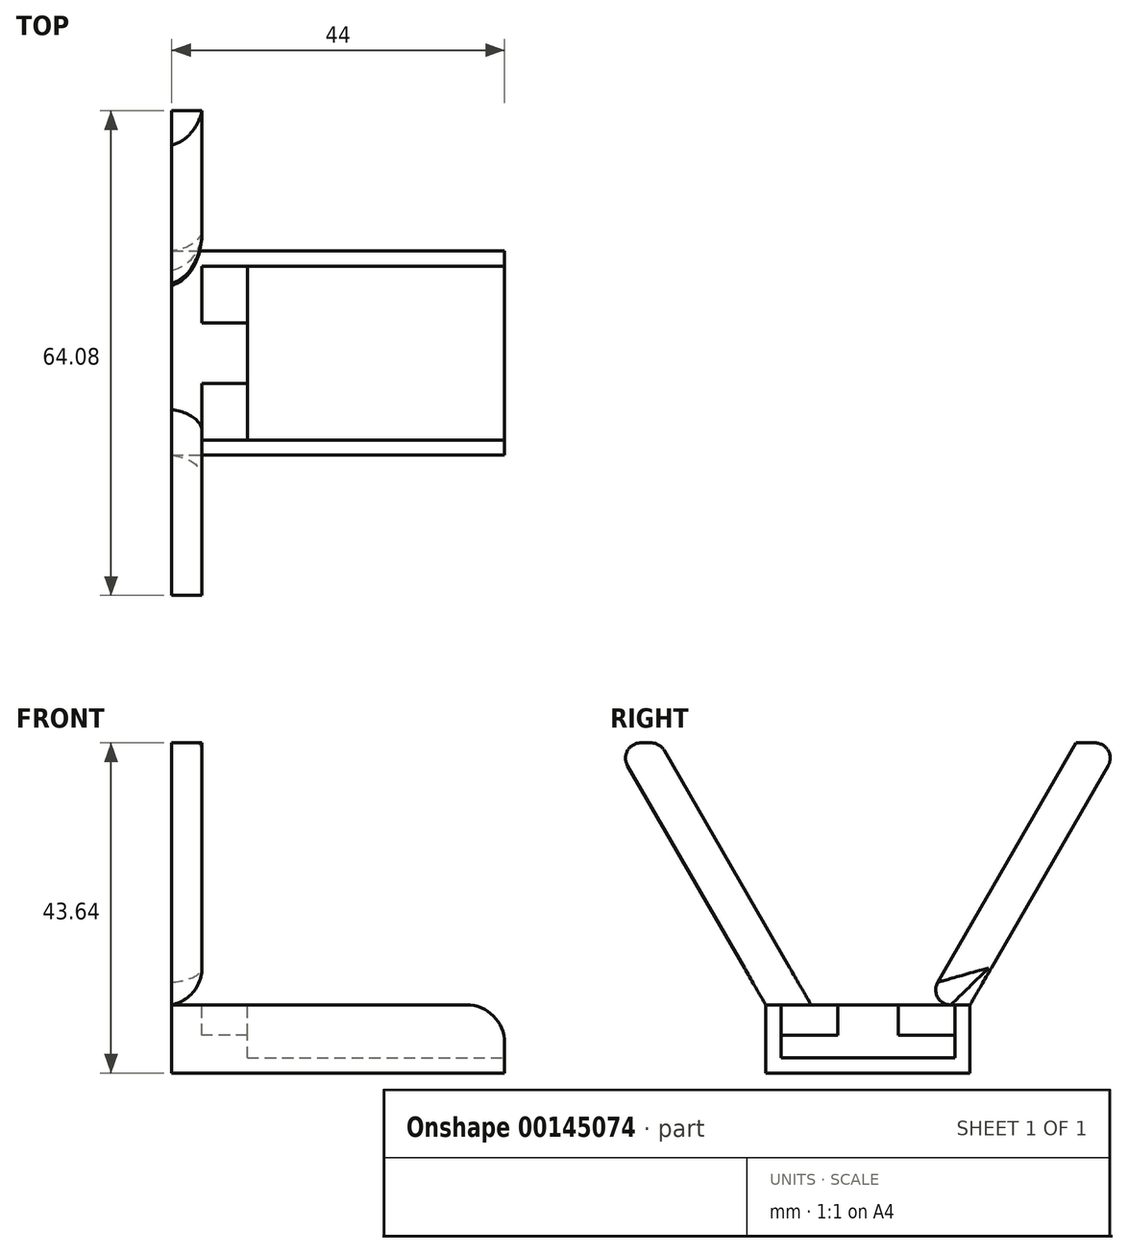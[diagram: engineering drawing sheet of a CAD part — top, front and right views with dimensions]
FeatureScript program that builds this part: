
annotation { "Feature Type Name" : "Feature", "Feature Type Description" : "" }
export const myFeature = defineFeature(function(context is Context, id is Id, definition is map)
    precondition{}
    {
        {
            var Q0;
            Q0=qCreatedBy(makeId("Top.planeOp"),FACE);
            var sketch = newSketch(context, id + "F0", { "sketchPlane" : qUnion([Q0])});
            skLineSegment(sketch, "E0.bottom", {"start": v(-23, 13.5) * mm, "end": v(21, 13.5) * mm});
            skLineSegment(sketch, "E0.top", {"start": v(-23, -13.5) * mm, "end": v(21, -13.5) * mm});
            skLineSegment(sketch, "E0.left", {"start": v(-23, 13.5) * mm, "end": v(-23, -13.5) * mm});
            skLineSegment(sketch, "E0.right", {"start": v(21, 13.5) * mm, "end": v(21, -13.5) * mm});
            skSolve(sketch);
        }
        {
            var Q0;
            Q0 = qSketchRegion(id + "F0", true);
            extrude(context, id + "F1", {"entities" : qUnion([Q0]), "oppositeDirection" : true, "depth" : 9 * mm});
        }
        {
            var Q0;
            Q0=qCreatedBy(makeId("Top.planeOp"),FACE);
            var sketch = newSketch(context, id + "F2", { "sketchPlane" : qUnion([Q0])});
            skLineSegment(sketch, "E1.bottom", {"start": v(-13, 11.5) * mm, "end": v(21, 11.5) * mm});
            skLineSegment(sketch, "E1.top", {"start": v(-13, -11.5) * mm, "end": v(21, -11.5) * mm});
            skLineSegment(sketch, "E1.left", {"start": v(-13, 11.5) * mm, "end": v(-13, -11.5) * mm});
            skLineSegment(sketch, "E1.right", {"start": v(21, 11.5) * mm, "end": v(21, -11.5) * mm});
            skSolve(sketch);
        }
        {
            var Q0;
            Q0 = qSketchRegion(id + "F2", true);
            extrude(context, id + "F3", {"entities" : qUnion([Q0]), "oppositeDirection" : true, "depth" : 7 * mm});
        }
        {
            var Q0;
            Q0=makeQuery(id+"F3.opExtrude","SWEPT_BODY",BODY,{"disambiguationData":[OSD([sQuery(id+"F2.wireOp",EDGE,"E1.bottom"),sQuery(id+"F2.wireOp",EDGE,"E1.top"),sQuery(id+"F2.wireOp",EDGE,"E1.left"),sQuery(id+"F2.wireOp",EDGE,"E1.right")])]});
            var Q1;
            Q1=makeQuery(id+"F1.opExtrude","SWEPT_BODY",BODY,{"disambiguationData":[OSD([sQuery(id+"F0.wireOp",EDGE,"E0.bottom"),sQuery(id+"F0.wireOp",EDGE,"E0.top"),sQuery(id+"F0.wireOp",EDGE,"E0.left"),sQuery(id+"F0.wireOp",EDGE,"E0.right")])]});
            booleanBodies(context, id + "F4", {"operationType" : BooleanOperationType.SUBTRACTION, "tools" : qUnion([Q0]), "targets" : qUnion([Q1])});
        }
        {
            var Q0;
            Q0=qCreatedBy(makeId("Top.planeOp"),FACE);
            var sketch = newSketch(context, id + "F5", { "sketchPlane" : qUnion([Q0])});
            skLineSegment(sketch, "E2.bottom", {"start": v(-13, 11.5) * mm, "end": v(-19, 11.5) * mm});
            skLineSegment(sketch, "E2.top", {"start": v(-13, 4) * mm, "end": v(-19, 4) * mm});
            skLineSegment(sketch, "E2.left", {"start": v(-13, 11.5) * mm, "end": v(-13, 4) * mm});
            skLineSegment(sketch, "E2.right", {"start": v(-19, 11.5) * mm, "end": v(-19, 4) * mm});
            skSolve(sketch);
        }
        {
            var Q0;
            Q0=qCreatedBy(makeId("Top.planeOp"),FACE);
            var sketch = newSketch(context, id + "F6", { "sketchPlane" : qUnion([Q0])});
            skLineSegment(sketch, "E3.bottom", {"start": v(-13, -4) * mm, "end": v(-19, -4) * mm});
            skLineSegment(sketch, "E3.top", {"start": v(-13, -11.5) * mm, "end": v(-19, -11.5) * mm});
            skLineSegment(sketch, "E3.left", {"start": v(-13, -4) * mm, "end": v(-13, -11.5) * mm});
            skLineSegment(sketch, "E3.right", {"start": v(-19, -4) * mm, "end": v(-19, -11.5) * mm});
            skSolve(sketch);
        }
        {
            var Q0;
            Q0 = qSketchRegion(id + "F6", true);
            var Q1;
            Q1 = qSketchRegion(id + "F5", true);
            extrude(context, id + "F7", {"entities" : qUnion([Q0, Q1]), "oppositeDirection" : true, "depth" : 4 * mm});
        }
        {
            var Q0;
            Q0=makeQuery(id+"F7.opExtrude","SWEPT_BODY",BODY,{"disambiguationData":[OSD([sQuery(id+"F5.wireOp",EDGE,"E2.bottom"),sQuery(id+"F5.wireOp",EDGE,"E2.top"),sQuery(id+"F5.wireOp",EDGE,"E2.left"),sQuery(id+"F5.wireOp",EDGE,"E2.right")])]});
            var Q1;
            Q1=makeQuery(id+"F7.opExtrude","SWEPT_BODY",BODY,{"disambiguationData":[OSD([sQuery(id+"F6.wireOp",EDGE,"E3.bottom"),sQuery(id+"F6.wireOp",EDGE,"E3.top"),sQuery(id+"F6.wireOp",EDGE,"E3.left"),sQuery(id+"F6.wireOp",EDGE,"E3.right")])]});
            var Q2;
            Q2=makeQuery(id+"F1.opExtrude","SWEPT_BODY",BODY,{"disambiguationData":[OSD([sQuery(id+"F0.wireOp",EDGE,"E0.bottom"),sQuery(id+"F0.wireOp",EDGE,"E0.top"),sQuery(id+"F0.wireOp",EDGE,"E0.left"),sQuery(id+"F0.wireOp",EDGE,"E0.right")])]});
            booleanBodies(context, id + "F8", {"operationType" : BooleanOperationType.SUBTRACTION, "tools" : qUnion([Q0, Q1]), "targets" : qUnion([Q2])});
        }
        {
            var Q0;
            Q0=makeQuery(id+"F1.opExtrude","SWEPT_FACE",FACE,{"disambiguationData":[OSD([sQuery(id+"F0.wireOp",EDGE,"E0.left")])]});
            var sketch = newSketch(context, id + "F9", { "sketchPlane" : qUnion([Q0])});
            skLineSegment(sketch, "E4", {"start": v(13.5, 0) * mm, "end": v(33.5, 34.64) * mm});
            skLineSegment(sketch, "E5", {"start": v(33.5, 34.64) * mm, "end": v(-33.5, 34.64) * mm});
            skLineSegment(sketch, "E6", {"start": v(-33.5, 34.64) * mm, "end": v(-13.5, 0) * mm});
            skLineSegment(sketch, "E7", {"start": v(-13.5, 0) * mm, "end": v(13.5, 0) * mm});
            skSolve(sketch);
        }
        {
            var Q0;
            Q0 = qSketchRegion(id + "F9", true);
            extrude(context, id + "F10", {"entities" : qUnion([Q0]), "oppositeDirection" : true, "depth" : 4 * mm});
        }
        {
            var Q0;
            Q0=makeQuery(id+"F9.imprint","IMPRINT",FACE,{"disambiguationData":[TD([[makeQuery(id+"F9.imprint","IMPRINT",EDGE,{"derivedFrom":sQuery(id+"F9.wireOp",EDGE,"E4")}),1.0]])]});
            var sketch = newSketch(context, id + "F11", { "sketchPlane" : qUnion([Q0])});
            skLineSegment(sketch, "E8", {"start": v(7.5, 0) * mm, "end": v(27.5, 34.64) * mm});
            skLineSegment(sketch, "E9", {"start": v(27.5, 34.64) * mm, "end": v(-27.5, 34.64) * mm});
            skLineSegment(sketch, "E10", {"start": v(-27.5, 34.64) * mm, "end": v(-7.5, 0) * mm});
            skLineSegment(sketch, "E11", {"start": v(-7.5, 0) * mm, "end": v(7.5, 0) * mm});
            skSolve(sketch);
        }
        {
            var Q0;
            Q0 = qSketchRegion(id + "F11", true);
            extrude(context, id + "F12", {"entities" : qUnion([Q0]), "oppositeDirection" : true, "depth" : 5 * mm});
        }
        {
            var Q0;
            Q0=makeQuery(id+"F12.opExtrude","SWEPT_BODY",BODY,{"disambiguationData":[OSD([sQuery(id+"F11.wireOp",EDGE,"E8"),sQuery(id+"F11.wireOp",EDGE,"E9"),sQuery(id+"F11.wireOp",EDGE,"E10"),sQuery(id+"F11.wireOp",EDGE,"E11")])]});
            var Q1;
            Q1=makeQuery(id+"F10.opExtrude","SWEPT_BODY",BODY,{"disambiguationData":[OSD([sQuery(id+"F9.wireOp",EDGE,"E4"),sQuery(id+"F9.wireOp",EDGE,"E5"),sQuery(id+"F9.wireOp",EDGE,"E6"),sQuery(id+"F9.wireOp",EDGE,"E7")])]});
            booleanBodies(context, id + "F13", {"operationType" : BooleanOperationType.SUBTRACTION, "tools" : qUnion([Q0]), "targets" : qUnion([Q1])});
        }
        {
            var Q0;
            Q0=makeQuery(id+"F10.opExtrude","SWEPT_EDGE",EDGE,{"disambiguationData":[OSD([sQuery(id+"F9.wireOp",EDGE,"E5"),sQuery(id+"F9.wireOp",EDGE,"E6")])]});
            var Q1;
            Q1=makeQuery(id+"F13.opBoolean","COPY",EDGE,{"derivedFrom":makeQuery(id+"F12.opExtrude","SWEPT_EDGE",EDGE,{"disambiguationData":[OSD([sQuery(id+"F9.wireOp",EDGE,"E5"),sQuery(id+"F11.wireOp",EDGE,"E9"),sQuery(id+"F11.wireOp",EDGE,"E10")])]})});
            var Q2;
            Q2=makeQuery(id+"F13.opBoolean","COPY",EDGE,{"derivedFrom":makeQuery(id+"F12.opExtrude","SWEPT_EDGE",EDGE,{"disambiguationData":[OSD([sQuery(id+"F9.wireOp",EDGE,"E5"),sQuery(id+"F11.wireOp",EDGE,"E8"),sQuery(id+"F11.wireOp",EDGE,"E9")])]})});
            var Q3;
            Q3=makeQuery(id+"F10.opExtrude","SWEPT_EDGE",EDGE,{"disambiguationData":[OSD([sQuery(id+"F9.wireOp",EDGE,"E4"),sQuery(id+"F9.wireOp",EDGE,"E5")])]});
            var Q4;
            Q4=makeQuery(id+"F13.opBoolean","COPY",EDGE,{"derivedFrom":makeQuery(id+"F12.opExtrude","SWEPT_EDGE",EDGE,{"disambiguationData":[OSD([sQuery(id+"F9.wireOp",EDGE,"E7"),sQuery(id+"F11.wireOp",EDGE,"E8"),sQuery(id+"F11.wireOp",EDGE,"E11")])]})});
            var Q5;
            Q5=makeQuery(id+"F13.opBoolean","COPY",EDGE,{"derivedFrom":makeQuery(id+"F12.opExtrude","SWEPT_EDGE",EDGE,{"disambiguationData":[OSD([sQuery(id+"F9.wireOp",EDGE,"E7"),sQuery(id+"F11.wireOp",EDGE,"E10"),sQuery(id+"F11.wireOp",EDGE,"E11")])]})});
            var Q6;
            Q6=makeQuery(id+"F4.opBoolean","COPY",EDGE,{"derivedFrom":makeQuery(id+"F3.opExtrude","CAP_EDGE",EDGE,{"disambiguationData":[OSD([sQuery(id+"F2.wireOp",EDGE,"E1.left")])],"isStart":true})});
            var Q7;
            Q7=makeQuery(id+"F8.opBoolean","COPY",EDGE,{"derivedFrom":makeQuery(id+"F7.opExtrude","CAP_EDGE",EDGE,{"disambiguationData":[OSD([sQuery(id+"F5.wireOp",EDGE,"E2.left")])],"isStart":false})});
            var Q8;
            Q8=makeQuery(id+"F8.opBoolean","COPY",EDGE,{"derivedFrom":makeQuery(id+"F7.opExtrude","CAP_EDGE",EDGE,{"disambiguationData":[OSD([sQuery(id+"F6.wireOp",EDGE,"E3.left")])],"isStart":false})});
            fillet(context, id + "F14", {"entities" : qUnion([Q0, Q1, Q2, Q3, Q4, Q5, Q6, Q7, Q8]), "radius" : 2 * mm, "tangentPropagation" : true, "allowEdgeOverflow" : false});
        }
        {
            var Q0;
            {var subQ0=sQuery(id+"F9.wireOp",EDGE,"E4");var subQ1=sQuery(id+"F9.wireOp",EDGE,"E7");Q0=makeQuery(id+"F13.opBoolean","SPLIT",EDGE,{"disambiguationData":[TD([makeQuery(id+"F10.opExtrude","SWEPT_FACE",FACE,{"disambiguationData":[OSD([subQ0])]})])],"derivedFrom":makeQuery(id+"F10.opExtrude","CAP_EDGE",EDGE,{"disambiguationData":[OSD([subQ1])],"isStart":false})});}
            var Q1;
            {var subQ0=sQuery(id+"F9.wireOp",EDGE,"E7");var subQ1=sQuery(id+"F9.wireOp",EDGE,"E6");Q1=makeQuery(id+"F13.opBoolean","SPLIT",EDGE,{"disambiguationData":[TD([makeQuery(id+"F10.opExtrude","SWEPT_FACE",FACE,{"disambiguationData":[OSD([subQ1])]})])],"derivedFrom":makeQuery(id+"F10.opExtrude","CAP_EDGE",EDGE,{"disambiguationData":[OSD([subQ0])],"isStart":false})});}
            var Q2;
            {var subQ0=sQuery(id+"F0.wireOp",EDGE,"E0.bottom");var subQ1=sQuery(id+"F0.wireOp",EDGE,"E0.right");Q2=makeQuery(id+"F4.opBoolean","SPLIT",EDGE,{"disambiguationData":[TD([makeQuery(id+"F1.opExtrude","SWEPT_FACE",FACE,{"disambiguationData":[OSD([subQ0])]})])],"derivedFrom":makeQuery(id+"F1.opExtrude","CAP_EDGE",EDGE,{"disambiguationData":[OSD([subQ1])],"isStart":true})});}
            var Q3;
            {var subQ0=sQuery(id+"F0.wireOp",EDGE,"E0.right");var subQ1=sQuery(id+"F0.wireOp",EDGE,"E0.top");Q3=makeQuery(id+"F4.opBoolean","SPLIT",EDGE,{"disambiguationData":[TD([makeQuery(id+"F1.opExtrude","SWEPT_FACE",FACE,{"disambiguationData":[OSD([subQ1])]})])],"derivedFrom":makeQuery(id+"F1.opExtrude","CAP_EDGE",EDGE,{"disambiguationData":[OSD([subQ0])],"isStart":true})});}
            fillet(context, id + "F15", {"entities" : qUnion([Q0, Q1, Q2, Q3]), "radius" : 5 * mm, "tangentPropagation" : true, "allowEdgeOverflow" : false});
        }
    });
